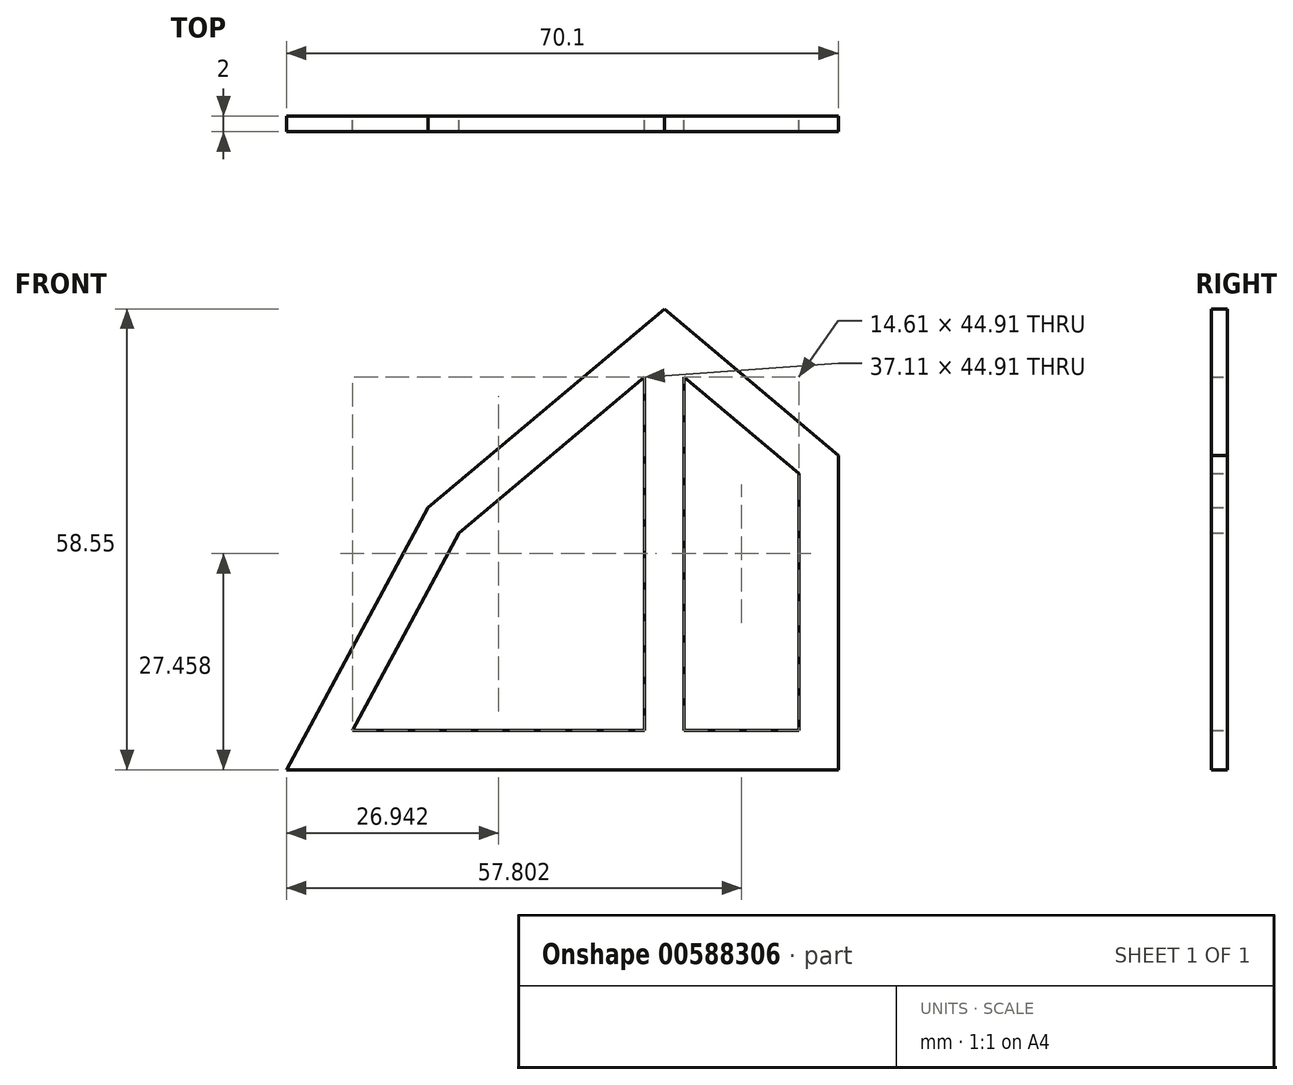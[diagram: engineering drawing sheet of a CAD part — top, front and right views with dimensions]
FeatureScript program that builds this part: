
annotation { "Feature Type Name" : "Feature", "Feature Type Description" : "" }
export const myFeature = defineFeature(function(context is Context, id is Id, definition is map)
    precondition{}
    {
        {
            var Q0;
            Q0=qCreatedBy(makeId("Front.planeOp"),FACE);
            var sketch = newSketch(context, id + "F0", { "sketchPlane" : qUnion([Q0])});
            skLineSegment(sketch, "E0", {"start": v(-54.04, 70.03) * mm, "end": v(-31.94, 51.43) * mm});
            skLineSegment(sketch, "E1", {"start": v(-54.04, 70.03) * mm, "end": v(-84.04, 44.78) * mm});
            skLineSegment(sketch, "E2", {"start": v(-102.04, 11.48) * mm, "end": v(-84.04, 44.78) * mm});
            skLineSegment(sketch, "E3", {"start": v(-102.04, 11.48) * mm, "end": v(-6.04, 11.48) * mm});
            skLineSegment(sketch, "E4", {"start": v(-102.04, 11.48) * mm, "end": v(-31.94, 11.48) * mm});
            skLineSegment(sketch, "E5", {"start": v(-31.94, 11.48) * mm, "end": v(-31.94, 51.43) * mm});
            skLineSegment(sketch, "E6.0", {"start": v(-93.66, 16.48) * mm, "end": v(-80.1, 41.57) * mm});
            skLineSegment(sketch, "E6.1", {"start": v(-56.54, 61.4) * mm, "end": v(-80.1, 41.57) * mm});
            skLineSegment(sketch, "E6.2", {"start": v(-93.66, 16.48) * mm, "end": v(-56.54, 16.48) * mm});
            skLineSegment(sketch, "E6.3", {"start": v(-36.94, 16.48) * mm, "end": v(-36.94, 49.1) * mm});
            skLineSegment(sketch, "E6.4", {"start": v(-51.54, 61.4) * mm, "end": v(-36.94, 49.1) * mm});
            skLineSegment(sketch, "E7", {"start": v(-51.54, 16.48) * mm, "end": v(-51.54, 61.4) * mm});
            skLineSegment(sketch, "E8", {"start": v(-56.54, 16.48) * mm, "end": v(-56.54, 61.4) * mm});
            skLineSegment(sketch, "E9.trimOffspring", {"start": v(-51.54, 16.48) * mm, "end": v(-36.94, 16.48) * mm});
            skSolve(sketch);
        }
        {
            var Q0;
            Q0=makeQuery(id+"F0.imprint","IMPRINT",FACE,{"disambiguationData":[TD([[makeQuery(id+"F0.imprint","IMPRINT",EDGE,{"derivedFrom":sQuery(id+"F0.wireOp",EDGE,"E0")}),-1.0]])]});
            extrude(context, id + "F1", {"entities" : qUnion([Q0]), "depth" : 2 * mm, "offsetDistance" : 25 * mm});
        }
    });
